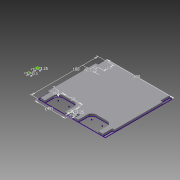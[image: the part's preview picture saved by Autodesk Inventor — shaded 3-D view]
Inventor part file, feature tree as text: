
AUTODESK INVENTOR PART (.ipt)
format: ipt  version: 2013 (Build 170138000, 138)  size: 122,368 bytes
history: native  units: mm
features: extrude x2, sketch x1
ambient origin geometry x8: Origin, YZ Plane, XZ Plane, XY Plane, X Axis, Y Axis, Z Axis, Center Point
feature tree (3):
  sketch  "Sketch1"  dims[d0=100.0mm d2=100.0mm d3=3.0mm d5=3.0mm d7=3.25mm d8=14.0mm d15=30.0mm d16=20.0mm d17=10.0mm d18=3.25mm d19=0.0mm d20=3.25mm d21=8.0mm d22=5.0mm d23=3.25mm d24=0.0mm d25=45.0mm d26=7.0mm]
  extrude  "Extrusion2"  Depth=100.0mm
  extrude  "Extrusion3"  Depth=3.0mm
